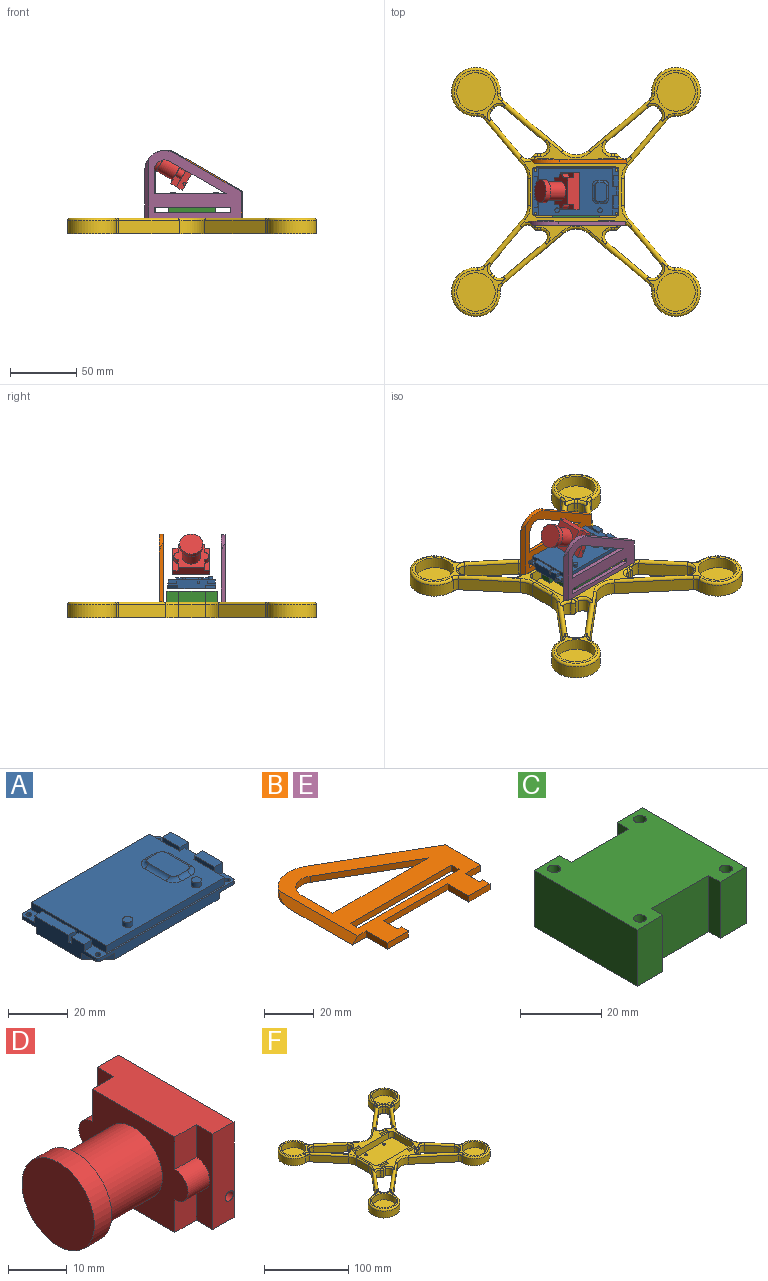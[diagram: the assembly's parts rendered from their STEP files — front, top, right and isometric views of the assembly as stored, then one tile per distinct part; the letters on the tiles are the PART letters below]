
ASSEMBLY  parts=6 mates=2
PART A: 60 faces, bbox 65x36.5x9 mm
  f0: plane 58.7x35.6mm, normal (0,0,1), area 1787.7mm2, adj f1,f24,f25,f26,f27,f29,f31,f48
  f1: plane 15x3mm, normal (1,0,0), area 45mm2, adj f0,f2,f26,f50
  f2: plane 65x36.5mm, normal (0,0,1), area 195mm2, adj f1,f6,f7,f8,f9,f10,f11,f12
  f3: plane 7.67x7.67mm, normal (0,0,-1), area 26mm2, adj f9,f10,f11,f16,f23
  f4: plane 7.67x7.67mm, normal (0,0,-1), area 26mm2, adj f11,f12,f15,f17,f22
  f5: plane 7.67x7.67mm, normal (0,0,-1), area 26mm2, adj f7,f8,f9,f13,f20
  f6: cylinder r=1mm len=1.4mm, axis (0,0,-1), area 2.2mm2, adj f2,f7,f17,f18
  f7: plane 63x4mm, normal (0,1,0), area 217.3mm2, adj f2,f5,f6,f8,f18,f19,f20,f21
  f8: cylinder r=1mm len=1.4mm, axis (0,0,-1), area 2.2mm2, adj f2,f5,f7,f9
  f9: plane 34.5x6.8mm, normal (-1,0,0), area 164.9mm2, adj f2,f3,f5,f8,f10,f19,f20,f23
  f10: cylinder r=1mm len=1.4mm, axis (0,0,-1), area 2.2mm2, adj f2,f3,f9,f11
  f11: plane 63x4mm, normal (0,-1,0), area 217.3mm2, adj f2,f3,f4,f10,f12,f19,f22,f23
  f12: cylinder r=1mm len=1.4mm, axis (0,0,-1), area 2.2mm2, adj f2,f4,f11,f17
  f13: cylinder r=1mm len=2mm, axis (0,0,-1), area 8.8mm2, adj f2,f5
  f14: cylinder r=1mm len=2mm, axis (0,0,-1), area 8.8mm2, adj f2,f18
  f15: cylinder r=1mm len=2mm, axis (0,0,-1), area 8.8mm2, adj f2,f4
  f16: cylinder r=1mm len=2mm, axis (0,0,-1), area 8.8mm2, adj f2,f3
  f17: plane 34.5x8.3mm, normal (1,0,0), area 179.9mm2, adj f2,f4,f6,f12,f18,f19,f21,f22
  f18: plane 7.67x7.67mm, normal (0,0,-1), area 26mm2, adj f6,f7,f14,f17,f21
  f19: plane 65x36.5mm, normal (0,0,-1), area 2254.9mm2, adj f7,f9,f11,f17,f20,f21,f22,f23
  f20: plane 7.67x7.67mm, normal (-0.71,0.71,0), area 28.2mm2, adj f5,f7,f9,f19
  f21: plane 7.67x7.67mm, normal (0.71,0.71,0), area 28.2mm2, adj f7,f17,f18,f19
  f22: plane 7.67x7.67mm, normal (0.71,-0.71,0), area 28.2mm2, adj f4,f11,f17,f19
  f23: plane 7.67x7.67mm, normal (-0.71,-0.71,0), area 28.2mm2, adj f3,f9,f11,f19
  f24: plane 14x3mm, normal (1,0,0), area 42mm2, adj f0,f2,f25,f49
  f25: plane 56x3mm, normal (0,1,0), area 168mm2, adj f0,f2,f24,f27
  f26: plane 56x3mm, normal (0,-1,0), area 168mm2, adj f0,f1,f2,f27
  f27: plane 35.6x3mm, normal (-1,0,0), area 106.8mm2, adj f0,f2,f25,f26
  f28: plane 3.5x3.5mm, normal (0,0,1), area 9.6mm2, adj f29
  f29: cylinder r=1.75mm len=3.5mm, axis (0,0,-1), area 22mm2, adj f0,f28
  f30: plane 3.5x3.5mm, normal (0,0,1), area 9.6mm2, adj f31
  f31: cylinder r=1.75mm len=3.5mm, axis (0,0,-1), area 22mm2, adj f0,f30
  f32: plane 16x3.7mm, normal (0,0,1), area 59.2mm2, adj f9,f33,f34,f35
  f33: plane 3.7x2.8mm, normal (0,1,0), area 10.4mm2, adj f2,f9,f32,f34
  f34: plane 16x2.8mm, normal (1,0,0), area 44.8mm2, adj f2,f32,f33,f35
  f35: plane 3.7x2.8mm, normal (0,-1,0), area 10.4mm2, adj f2,f9,f32,f34
  f36: plane 6x3.7mm, normal (0,0,1), area 22.2mm2, adj f9,f37,f38,f39
  f37: plane 3.7x2.8mm, normal (0,1,0), area 10.4mm2, adj f2,f9,f36,f38
  f38: plane 6x2.8mm, normal (1,0,0), area 16.8mm2, adj f2,f36,f37,f39
  f39: plane 3.7x2.8mm, normal (0,-1,0), area 10.4mm2, adj f2,f9,f36,f38
  f40: plane 9.5x4mm, normal (0,0,1), area 38mm2, adj f17,f41,f42,f43
  f41: plane 4.3x4mm, normal (0,-1,0), area 17.2mm2, adj f2,f17,f40,f42
  f42: plane 9.5x4.3mm, normal (-1,0,0), area 40.9mm2, adj f2,f40,f41,f43
  f43: plane 4.3x4mm, normal (0,1,0), area 17.2mm2, adj f2,f17,f40,f42
  f44: plane 8.3x4mm, normal (0,0,1), area 33.2mm2, adj f17,f45,f46,f47
  f45: plane 4.3x4mm, normal (0,1,0), area 17.2mm2, adj f2,f17,f44,f47
  f46: plane 4.3x4mm, normal (0,-1,0), area 17.2mm2, adj f2,f17,f44,f47
  f47: plane 8.3x4.3mm, normal (-1,0,0), area 35.7mm2, adj f2,f44,f45,f46
  f48: plane 6.6x3mm, normal (1,0,0), area 19.8mm2, adj f0,f2,f49,f50
  f49: plane 3x2.7mm, normal (0,1,0), area 8.1mm2, adj f0,f2,f24,f48
  f50: plane 3x2.7mm, normal (0,-1,0), area 8.1mm2, adj f0,f1,f2,f48
  f51: plane 14x8.5mm, normal (0,0,1), area 115.6mm2, adj f52,f53,f54,f55,f56,f57,f58,f59
  f52: cylinder r=2mm len=4.5mm, axis (1,0,0), area 10.9mm2, adj f0,f51,f53,f54
  f53: torus R=3.87mm, axis (0,0,1), area 10.7mm2, adj f0,f51,f52,f55
  f54: torus R=3.87mm, axis (0,0,1), area 10.7mm2, adj f0,f51,f52,f56
  f55: cylinder r=2mm len=10mm, axis (0,1,0), area 24.3mm2, adj f0,f51,f53,f57
  f56: cylinder r=2mm len=10mm, axis (0,-1,0), area 24.3mm2, adj f0,f51,f54,f58
  f57: torus R=3.87mm, axis (0,0,1), area 10.7mm2, adj f0,f51,f55,f59
  f58: torus R=3.87mm, axis (0,0,1), area 10.7mm2, adj f0,f51,f56,f59
  f59: cylinder r=2mm len=4.5mm, axis (1,0,0), area 10.9mm2, adj f0,f51,f57,f58
PART B: 28 faces, bbox 73x63.1x3 mm
  f0: plane 8x3mm, normal (1,0,0), area 24mm2, adj f1,f24,f25,f26
  f1: plane 36.5x3mm, normal (0,-1,0), area 109.5mm2, adj f0,f2,f25,f26
  f2: plane 12x3mm, normal (-1,0,0), area 36mm2, adj f1,f3,f25,f26
  f3: plane 12x3mm, normal (0,-1,0), area 36mm2, adj f2,f4,f25,f26
  f4: plane 4x3mm, normal (1,0,0), area 12mm2, adj f3,f5,f25,f26
  f5: plane 3x2mm, normal (0,1,0), area 6mm2, adj f4,f6,f25,f26
  f6: plane 8x3mm, normal (1,0,0), area 24mm2, adj f5,f7,f25,f26
  f7: plane 8.5x3mm, normal (0,-1,0), area 25.5mm2, adj f6,f8,f25,f26
  f8: plane 20x3mm, normal (1,0,0), area 60mm2, adj f7,f9,f25,f26
  f9: plane 50.41x29.1mm, normal (0.5,0.87,0), area 174.6mm2, adj f8,f10,f25,f26
  f10: cylinder r=15mm len=22.43mm, axis (0,0,-1), area 75.8mm2, adj f9,f11,f25,f26,f27
  f11: cylinder r=33.51mm len=3.32mm, axis (0,0,-1), area 0.2mm2, adj f10,f26,f27
  f12: plane 8x3mm, normal (0,-1,0), area 19.5mm2, adj f13,f25,f26,f27
  f13: plane 12x3mm, normal (-1,0,0), area 36mm2, adj f12,f14,f25,f26
  f14: plane 12x3mm, normal (0,-1,0), area 36mm2, adj f13,f15,f25,f26
  f15: plane 4x3mm, normal (1,0,0), area 12mm2, adj f14,f24,f25,f26
  f16: plane 4.38x3mm, normal (-1,0,0), area 13.1mm2, adj f17,f22,f25,f26
  f17: plane 57.57x3mm, normal (0,1,0), area 172.7mm2, adj f16,f18,f25,f26
  f18: plane 4.38x3mm, normal (1,0,0), area 13.1mm2, adj f17,f22,f25,f26
  f19: plane 54.56x3mm, normal (0,1,0), area 163.7mm2, adj f20,f23,f25,f26
  f20: plane 17.86x3mm, normal (1,0,0), area 53.6mm2, adj f19,f21,f25,f26
  f21: cylinder r=7.88mm len=11.82mm, axis (0,0,-1), area 49.5mm2, adj f20,f23,f25,f26
  f22: plane 57.57x3mm, normal (0,-1,0), area 172.7mm2, adj f16,f18,f25,f26
  f23: plane 42.74x24.68mm, normal (-0.5,-0.87,0), area 148.1mm2, adj f19,f21,f25,f26
  f24: plane 3x2mm, normal (0,1,0), area 6mm2, adj f0,f15,f25,f26
  f25: plane 70x63.11mm, normal (0,0,1), area 1903.1mm2, adj f0,f1,f2,f3,f4,f5,f6,f7
  f26: plane 73x63.11mm, normal (0,0,-1), area 2029mm2, adj f0,f1,f2,f3,f4,f5,f6,f7
  f27: plane 44.99x3mm, normal (-0.71,0,0.71), area 178.1mm2, adj f10,f11,f12,f25,f26
PART C: 18 faces, bbox 38x36x17 mm
  f0: plane 36x17.02mm, normal (1,0,0), area 612.6mm2, adj f1,f15,f16,f17
  f1: plane 17.02x9mm, normal (0,1,0), area 153.2mm2, adj f0,f2,f16,f17
  f2: plane 17.02x4mm, normal (-1,0,0), area 68.1mm2, adj f1,f3,f16,f17
  f3: plane 20x17.02mm, normal (0,1,0), area 340.4mm2, adj f2,f4,f16,f17
  f4: plane 17.02x4mm, normal (1,0,0), area 68.1mm2, adj f3,f5,f16,f17
  f5: plane 17.02x9mm, normal (0,1,0), area 153.2mm2, adj f4,f6,f16,f17
  f6: plane 36x17.02mm, normal (-1,0,0), area 612.6mm2, adj f5,f7,f16,f17
  f7: plane 17.02x9mm, normal (0,-1,0), area 153.2mm2, adj f6,f8,f16,f17
  f8: plane 17.02x4mm, normal (1,0,0), area 68.1mm2, adj f7,f9,f16,f17
  f9: plane 20x17.02mm, normal (0,-1,0), area 340.4mm2, adj f8,f10,f16,f17
  f10: plane 17.02x4mm, normal (-1,0,0), area 68.1mm2, adj f9,f15,f16,f17
  f11: cylinder r=1.6mm len=17.02mm, axis (0,0,-1), area 171.1mm2, adj f16,f17
  f12: cylinder r=1.6mm len=17.02mm, axis (0,0,-1), area 171.1mm2, adj f16,f17
  f13: cylinder r=1.6mm len=17.02mm, axis (0,0,-1), area 171.1mm2, adj f16,f17
  f14: cylinder r=1.6mm len=17.02mm, axis (0,0,-1), area 171.1mm2, adj f16,f17
  f15: plane 17.02x9mm, normal (0,-1,0), area 153.2mm2, adj f0,f10,f16,f17
  f16: plane 38x36mm, normal (0,0,1), area 1175.8mm2, adj f0,f1,f2,f3,f4,f5,f6,f7
  f17: plane 38x36mm, normal (0,0,-1), area 1175.8mm2, adj f0,f1,f2,f3,f4,f5,f6,f7
PART D: 22 faces, bbox 28.5x28.2x20 mm
  f0: plane 20x4.16mm, normal (-1,0,0), area 63.9mm2, adj f2,f4,f6,f12,f16,f17
  f1: plane 20x4mm, normal (-1,0,0), area 63.9mm2, adj f2,f5,f6,f13,f14,f15
  f2: plane 28x10.3mm, normal (0,0,1), area 246.8mm2, adj f0,f1,f3,f4,f5,f11,f15,f16
  f3: plane 28x20mm, normal (1,0,0), area 560mm2, adj f2,f4,f5,f6
  f4: plane 20x5.1mm, normal (0,1,0), area 98.9mm2, adj f0,f2,f3,f6,f10
  f5: plane 20x5.1mm, normal (0,-1,0), area 98.9mm2, adj f1,f2,f3,f6,f8
  f6: plane 28x10.3mm, normal (0,0,-1), area 246.8mm2, adj f0,f1,f3,f4,f5,f11,f12,f13
  f7: plane 2x2mm, normal (0,-1,0), area 3.1mm2, adj f8
  f8: cylinder r=1mm len=3mm, axis (0,-1,0), area 18.8mm2, adj f5,f7
  f9: plane 2x2mm, normal (0,1,0), area 3.1mm2, adj f10
  f10: cylinder r=1mm len=3mm, axis (0,1,0), area 18.8mm2, adj f4,f9
  f11: plane 27.36x20mm, normal (-1,0,0), area 278.2mm2, adj f2,f6,f12,f13,f14,f15,f16,f17
  f12: plane 6.8x5.2mm, normal (0,1,0), area 35.4mm2, adj f0,f6,f11,f17
  f13: plane 6.8x5.2mm, normal (0,-1,0), area 35.4mm2, adj f1,f6,f11,f14
  f14: cylinder r=3.2mm len=6.4mm, axis (1,0,0), area 52.3mm2, adj f1,f11,f13,f15
  f15: plane 6.8x5.2mm, normal (0,-1,0), area 35.4mm2, adj f1,f2,f11,f14
  f16: plane 6.8x5.2mm, normal (0,1,0), area 35.4mm2, adj f0,f2,f11,f17
  f17: extruded ~6.4x5.2mm, area 52.3mm2, adj f0,f11,f12,f16
  f18: cylinder r=7mm len=14mm, axis (1,0,0), area 615.8mm2, adj f11,f21
  f19: plane 17.5x17.5mm, normal (-1,0,0), area 240.5mm2, adj f20
  f20: cylinder r=8.75mm len=17.5mm, axis (1,0,0), area 230.9mm2, adj f19,f21
  f21: plane 17.5x17.5mm, normal (1,0,0), area 86.6mm2, adj f18,f20
PART E: same geometry as B
PART F: 171 faces, bbox 191.4x191.4x12 mm
  f0: plane 8x3.5mm, normal (-1,0,0), area 28mm2, adj f7,f55,f57,f170
  f1: plane 8x3.5mm, normal (-1,0,0), area 28mm2, adj f7,f59,f60,f168
  f2: plane 8x3.5mm, normal (-1,0,0), area 28mm2, adj f7,f62,f63,f164
  f3: plane 8x3.5mm, normal (-1,0,0), area 28mm2, adj f7,f64,f66,f166
  f4: plane 38.79x38.79mm, normal (0,0,1), area 226.8mm2, adj f46,f122,f126,f129,f133,f137,f157,f159
  f5: plane 38.79x38.79mm, normal (0,0,1), area 226.8mm2, adj f48,f141,f144,f147,f148,f151,f152,f154
  f6: plane 38.79x38.79mm, normal (0,0,1), area 226.8mm2, adj f44,f124,f127,f130,f131,f134,f135,f138
  f7: plane 84.28x78.72mm, normal (0,0,1), area 1391.4mm2, adj f0,f1,f2,f3,f25,f26,f27,f28
  f8: plane 38.79x38.79mm, normal (0,0,1), area 226.8mm2, adj f50,f108,f109,f111,f112,f115,f116,f119
  f9: plane 188.37x188.37mm, normal (0,0,-1), area 10299.6mm2, adj f10,f11,f12,f13,f14,f15,f16,f17
  f10: plane 35.64x29.9mm, normal (0.77,0.64,0), area 465.2mm2, adj f9,f34,f39,f139
  f11: plane 35.64x29.9mm, normal (0.77,-0.64,0), area 465.2mm2, adj f9,f35,f40,f154
  f12: plane 45.79x38.42mm, normal (-0.64,0.77,0), area 597.7mm2, adj f9,f36,f41,f141
  f13: plane 45.79x38.42mm, normal (0.64,0.77,0), area 597.7mm2, adj f9,f29,f41,f137
  f14: cylinder r=18.53mm len=37.05mm, axis (0,0,-1), area 903.2mm2, adj f9,f29,f30,f129
  f15: plane 35.64x29.9mm, normal (-0.77,-0.64,0), area 465.2mm2, adj f9,f30,f37,f122
  f16: plane 35.64x29.9mm, normal (-0.77,0.64,0), area 465.2mm2, adj f9,f31,f38,f108
  f17: cylinder r=18.53mm len=37.05mm, axis (0,0,-1), area 903.2mm2, adj f9,f31,f32,f115
  f18: plane 45.79x38.42mm, normal (0.64,-0.77,0), area 597.7mm2, adj f9,f32,f42,f120
  f19: plane 45.79x38.42mm, normal (-0.64,-0.77,0), area 597.7mm2, adj f9,f33,f42,f124
  f20: cylinder r=18.53mm len=37.05mm, axis (0,0,-1), area 903.2mm2, adj f9,f33,f34,f134
  f21: cylinder r=18.53mm len=37.05mm, axis (0,0,-1), area 903.2mm2, adj f9,f35,f36,f152
  f22: plane 20.3x10mm, normal (1,0,0), area 203mm2, adj f9,f39,f40,f149
  f23: plane 20.3x10mm, normal (-1,0,0), area 203mm2, adj f9,f37,f38,f118
  f24: plane 65x39mm, normal (0,0,1), area 2481.4mm2, adj f25,f26,f27,f28,f51,f52,f53,f54
  f25: plane 29x9mm, normal (1,0,0), area 261mm2, adj f7,f24,f51,f53
  f26: plane 55x9mm, normal (0,1,0), area 495mm2, adj f7,f24,f51,f52
  f27: plane 29x9mm, normal (-1,0,0), area 261mm2, adj f7,f24,f52,f54
  f28: plane 55x9mm, normal (0,-1,0), area 495mm2, adj f7,f24,f53,f54
  f29: cylinder r=5mm len=10mm, axis (0,0,-1), area 47.7mm2, adj f9,f13,f14,f133
  f30: cylinder r=5mm len=10mm, axis (0,0,-1), area 47.7mm2, adj f9,f14,f15,f126
  f31: cylinder r=5mm len=10mm, axis (0,0,-1), area 47.7mm2, adj f9,f16,f17,f111
  f32: cylinder r=5mm len=10mm, axis (0,0,-1), area 47.7mm2, adj f9,f17,f18,f119
  f33: cylinder r=5mm len=10mm, axis (0,0,-1), area 47.7mm2, adj f9,f19,f20,f130
  f34: cylinder r=5mm len=10mm, axis (0,0,-1), area 47.7mm2, adj f9,f10,f20,f138
  f35: cylinder r=5mm len=10mm, axis (0,0,-1), area 47.7mm2, adj f9,f11,f21,f155
  f36: cylinder r=5mm len=10mm, axis (0,0,-1), area 47.7mm2, adj f9,f12,f21,f148
  f37: cylinder r=15mm len=10mm, axis (0,0,1), area 104.7mm2, adj f9,f15,f23,f121
  f38: cylinder r=15mm len=10mm, axis (0,0,-1), area 104.7mm2, adj f9,f16,f23,f114
  f39: cylinder r=15mm len=10mm, axis (0,0,1), area 104.7mm2, adj f9,f10,f22,f145
  f40: cylinder r=15mm len=10mm, axis (0,0,-1), area 104.7mm2, adj f9,f11,f22,f153
  f41: cylinder r=15mm len=19.28mm, axis (0,0,-1), area 209.4mm2, adj f9,f12,f13,f142
  f42: cylinder r=15mm len=19.28mm, axis (0,0,-1), area 209.4mm2, adj f9,f18,f19,f123
  f43: plane 29.05x29.05mm, normal (0,0,1), area 662.8mm2, adj f44
  f44: cylinder r=14.53mm len=29.05mm, axis (0,0,1), area 821.4mm2, adj f6,f43
  f45: plane 29.05x29.05mm, normal (0,0,1), area 662.8mm2, adj f46
  f46: cylinder r=14.53mm len=29.05mm, axis (0,0,1), area 821.4mm2, adj f4,f45
  f47: plane 29.05x29.05mm, normal (0,0,1), area 662.8mm2, adj f48
  f48: cylinder r=14.53mm len=29.05mm, axis (0,0,1), area 821.4mm2, adj f5,f47
  f49: plane 29.05x29.05mm, normal (0,0,1), area 662.8mm2, adj f50
  f50: cylinder r=14.53mm len=29.05mm, axis (0,0,1), area 821.4mm2, adj f8,f49
  f51: cylinder r=5mm len=9mm, axis (0,0,-1), area 70.7mm2, adj f7,f24,f25,f26
  f52: cylinder r=5mm len=9mm, axis (0,0,1), area 70.7mm2, adj f7,f24,f26,f27
  f53: cylinder r=5mm len=9mm, axis (0,0,1), area 70.7mm2, adj f7,f24,f25,f28
  f54: cylinder r=5mm len=9mm, axis (0,0,-1), area 70.7mm2, adj f7,f24,f27,f28
  f55: plane 16x12mm, normal (0,-1,0), area 160mm2, adj f0,f7,f9,f56,f169,f170
  f56: plane 12x3.5mm, normal (1,0,0), area 42mm2, adj f7,f9,f55,f57
  f57: plane 16x12mm, normal (0,1,0), area 160mm2, adj f0,f7,f9,f56,f169,f170
  f58: plane 12x3.5mm, normal (1,0,0), area 42mm2, adj f7,f9,f59,f60
  f59: plane 16x12mm, normal (0,1,0), area 160mm2, adj f1,f7,f9,f58,f167,f168
  f60: plane 16x12mm, normal (0,-1,0), area 160mm2, adj f1,f7,f9,f58,f167,f168
  f61: plane 12x3.5mm, normal (1,0,0), area 42mm2, adj f7,f9,f62,f63
  f62: plane 16x12mm, normal (0,1,0), area 160mm2, adj f2,f7,f9,f61,f163,f164
  f63: plane 16x12mm, normal (0,-1,0), area 160mm2, adj f2,f7,f9,f61,f163,f164
  f64: plane 16x12mm, normal (0,-1,0), area 160mm2, adj f3,f7,f9,f65,f165,f166
  f65: plane 12x3.5mm, normal (1,0,0), area 42mm2, adj f7,f9,f64,f66
  f66: plane 16x12mm, normal (0,1,0), area 160mm2, adj f3,f7,f9,f65,f165,f166
  f67: cylinder r=1.6mm len=3.2mm, axis (0,0,-1), area 30.2mm2, adj f9,f24
  f68: cylinder r=1.6mm len=3.2mm, axis (0,0,-1), area 30.2mm2, adj f9,f24
  f69: cylinder r=1.6mm len=3.2mm, axis (0,0,-1), area 30.2mm2, adj f9,f24
  f70: cylinder r=1.6mm len=3.2mm, axis (0,0,-1), area 30.2mm2, adj f9,f24
  f71: cylinder r=18.53mm len=10mm, axis (0,0,1), area 26.1mm2, adj f9,f103,f106,f159
  f72: plane 27.96x23.46mm, normal (0.77,0.64,0), area 365mm2, adj f9,f105,f106,f122
  f73: plane 10x2.62mm, normal (0,1,0), area 26.2mm2, adj f9,f90,f104,f158
  f74: plane 31.27x26.24mm, normal (-0.64,-0.77,0), area 408.2mm2, adj f9,f103,f104,f137
  f75: cylinder r=18.53mm len=10mm, axis (0,0,1), area 26.1mm2, adj f9,f91,f94,f131
  f76: plane 27.96x23.46mm, normal (-0.77,-0.64,0), area 365mm2, adj f9,f93,f94,f139
  f77: plane 10x2.62mm, normal (0,-1,0), area 26.2mm2, adj f9,f87,f92,f128
  f78: plane 31.27x26.24mm, normal (0.64,0.77,0), area 408.2mm2, adj f9,f91,f92,f124
  f79: plane 27.96x23.46mm, normal (-0.77,0.64,0), area 365mm2, adj f9,f95,f98,f154
  f80: cylinder r=18.53mm len=10mm, axis (0,0,1), area 26.1mm2, adj f9,f97,f98,f147
  f81: plane 31.27x26.24mm, normal (0.64,-0.77,0), area 408.2mm2, adj f9,f96,f97,f141
  f82: plane 10x2.62mm, normal (0,1,0), area 26.2mm2, adj f9,f88,f96,f143
  f83: plane 27.96x23.46mm, normal (0.77,-0.64,0), area 365mm2, adj f9,f99,f102,f108
  f84: cylinder r=18.53mm len=10mm, axis (0,0,1), area 26.1mm2, adj f9,f99,f100,f112
  f85: plane 31.27x26.24mm, normal (-0.64,0.77,0), area 408.2mm2, adj f9,f100,f101,f120
  f86: plane 10x2.62mm, normal (0,-1,0), area 26.2mm2, adj f9,f89,f101,f113
  f87: cylinder r=4mm len=10mm, axis (0,0,1), area 39.6mm2, adj f9,f77,f93,f132
  f88: cylinder r=4mm len=10mm, axis (0,0,1), area 39.6mm2, adj f9,f82,f95,f146
  f89: cylinder r=4mm len=10mm, axis (0,0,1), area 39.6mm2, adj f9,f86,f102,f110
  f90: cylinder r=4mm len=10mm, axis (0,0,1), area 39.6mm2, adj f9,f73,f105,f160
  f91: cylinder r=5mm len=10mm, axis (0,0,1), area 77.7mm2, adj f9,f75,f78,f127
  f92: cylinder r=5mm len=10mm, axis (0,0,-1), area 122.2mm2, adj f9,f77,f78,f125
  f93: cylinder r=5mm len=10mm, axis (0,0,1), area 93.1mm2, adj f9,f76,f87,f136
  f94: cylinder r=5mm len=10mm, axis (0,0,1), area 77.7mm2, adj f9,f75,f76,f135
  f95: cylinder r=5mm len=10mm, axis (0,0,1), area 93.1mm2, adj f9,f79,f88,f150
  f96: cylinder r=5mm len=10mm, axis (0,0,-1), area 122.2mm2, adj f9,f81,f82,f140
  f97: cylinder r=5mm len=10mm, axis (0,0,1), area 77.7mm2, adj f9,f80,f81,f144
  f98: cylinder r=5mm len=10mm, axis (0,0,1), area 77.7mm2, adj f9,f79,f80,f151
  f99: cylinder r=5mm len=10mm, axis (0,0,1), area 77.7mm2, adj f9,f83,f84,f109
  f100: cylinder r=5mm len=10mm, axis (0,0,1), area 77.7mm2, adj f9,f84,f85,f116
  f101: cylinder r=5mm len=10mm, axis (0,0,-1), area 122.2mm2, adj f9,f85,f86,f117
  f102: cylinder r=5mm len=10mm, axis (0,0,1), area 93.1mm2, adj f9,f83,f89,f107
  f103: cylinder r=5mm len=10mm, axis (0,0,1), area 77.7mm2, adj f9,f71,f74,f157
  f104: cylinder r=5mm len=10mm, axis (0,0,-1), area 122.2mm2, adj f9,f73,f74,f156
  f105: cylinder r=5mm len=10mm, axis (0,0,1), area 93.1mm2, adj f9,f72,f90,f162
  f106: cylinder r=5mm len=10mm, axis (0,0,1), area 77.7mm2, adj f9,f71,f72,f161
  f107: torus R=7mm, axis (0,0,1), area 33.5mm2, adj f7,f102,f108,f110
  f108: cylinder r=2mm len=38.21mm, axis (0.64,0.77,0), area 260.8mm2, adj f7,f8,f16,f83,f107,f109,f111,f114
  f109: torus R=7mm, axis (0,0,1), area 28mm2, adj f8,f99,f108,f112
  f110: torus R=2mm, axis (0,0,1), area 10.2mm2, adj f7,f89,f107,f113
  f111: torus R=7mm, axis (0,0,1), area 17.2mm2, adj f8,f31,f108,f115
  f112: torus R=16.53mm, axis (0,0,1), area 7.9mm2, adj f8,f84,f109,f116
  f113: cylinder r=2mm len=2.62mm, axis (1,0,0), area 8.2mm2, adj f7,f86,f110,f117
  f114: torus R=17mm, axis (0,0,1), area 34.5mm2, adj f7,f38,f108,f118
  f115: torus R=16.53mm, axis (0,0,1), area 272.6mm2, adj f8,f17,f111,f119
  f116: torus R=7mm, axis (0,0,1), area 28mm2, adj f8,f100,f112,f120
  f117: torus R=7mm, axis (0,0,1), area 44mm2, adj f7,f101,f113,f120
  f118: cylinder r=2mm len=20.3mm, axis (0,1,0), area 63.8mm2, adj f7,f23,f114,f121
  f119: torus R=7mm, axis (0,0,1), area 17.2mm2, adj f8,f32,f115,f120
  f120: cylinder r=2mm len=48.36mm, axis (-0.77,-0.64,0), area 316mm2, adj f7,f8,f18,f85,f116,f117,f119,f123
  f121: torus R=17mm, axis (0,0,1), area 34.5mm2, adj f7,f37,f118,f122
  f122: cylinder r=2mm len=38.21mm, axis (-0.64,0.77,0), area 260.8mm2, adj f4,f7,f15,f72,f121,f126,f161,f162
  f123: torus R=17mm, axis (0,0,1), area 69mm2, adj f7,f42,f120,f124
  f124: cylinder r=2mm len=48.36mm, axis (-0.77,0.64,0), area 316mm2, adj f6,f7,f19,f78,f123,f125,f127,f130
  f125: torus R=7mm, axis (0,0,1), area 44mm2, adj f7,f92,f124,f128
  f126: torus R=7mm, axis (0,0,1), area 17.2mm2, adj f4,f30,f122,f129
  f127: torus R=7mm, axis (0,0,1), area 28mm2, adj f6,f91,f124,f131
  f128: cylinder r=2mm len=2.62mm, axis (1,0,0), area 8.2mm2, adj f7,f77,f125,f132
  f129: torus R=16.53mm, axis (0,0,1), area 272.6mm2, adj f4,f14,f126,f133
  f130: torus R=7mm, axis (0,0,1), area 17.2mm2, adj f6,f33,f124,f134
  f131: torus R=16.53mm, axis (0,0,1), area 7.9mm2, adj f6,f75,f127,f135
  f132: torus R=2mm, axis (0,0,1), area 10.2mm2, adj f7,f87,f128,f136
  f133: torus R=7mm, axis (0,0,1), area 17.2mm2, adj f4,f29,f129,f137
  f134: torus R=16.53mm, axis (0,0,1), area 272.6mm2, adj f6,f20,f130,f138
  f135: torus R=7mm, axis (0,0,1), area 28mm2, adj f6,f94,f131,f139
  f136: torus R=7mm, axis (0,0,1), area 33.5mm2, adj f7,f93,f132,f139
  f137: cylinder r=2mm len=48.36mm, axis (0.77,-0.64,0), area 316mm2, adj f4,f7,f13,f74,f133,f142,f156,f157
  f138: torus R=7mm, axis (0,0,1), area 17.2mm2, adj f6,f34,f134,f139
  f139: cylinder r=2mm len=38.21mm, axis (0.64,-0.77,0), area 260.8mm2, adj f6,f7,f10,f76,f135,f136,f138,f145
  f140: torus R=7mm, axis (0,0,1), area 44mm2, adj f7,f96,f141,f143
  f141: cylinder r=2mm len=48.36mm, axis (0.77,0.64,0), area 316mm2, adj f5,f7,f12,f81,f140,f142,f144,f148
  f142: torus R=17mm, axis (0,0,1), area 69mm2, adj f7,f41,f137,f141
  f143: cylinder r=2mm len=2.62mm, axis (-1,0,0), area 8.2mm2, adj f7,f82,f140,f146
  f144: torus R=7mm, axis (0,0,1), area 28mm2, adj f5,f97,f141,f147
  f145: torus R=17mm, axis (0,0,1), area 34.5mm2, adj f7,f39,f139,f149
  f146: torus R=2mm, axis (0,0,1), area 10.2mm2, adj f7,f88,f143,f150
  f147: torus R=16.53mm, axis (0,0,1), area 7.9mm2, adj f5,f80,f144,f151
  f148: torus R=7mm, axis (0,0,1), area 17.2mm2, adj f5,f36,f141,f152
  f149: cylinder r=2mm len=20.3mm, axis (0,-1,0), area 63.8mm2, adj f7,f22,f145,f153
  f150: torus R=7mm, axis (0,0,1), area 33.5mm2, adj f7,f95,f146,f154
  f151: torus R=7mm, axis (0,0,1), area 28mm2, adj f5,f98,f147,f154
  f152: torus R=16.53mm, axis (0,0,1), area 272.6mm2, adj f5,f21,f148,f155
  f153: torus R=17mm, axis (0,0,1), area 34.5mm2, adj f7,f40,f149,f154
  f154: cylinder r=2mm len=38.21mm, axis (-0.64,-0.77,0), area 260.8mm2, adj f5,f7,f11,f79,f150,f151,f153,f155
  f155: torus R=7mm, axis (0,0,1), area 17.2mm2, adj f5,f35,f152,f154
  f156: torus R=7mm, axis (0,0,1), area 44mm2, adj f7,f104,f137,f158
  f157: torus R=7mm, axis (0,0,1), area 28mm2, adj f4,f103,f137,f159
  f158: cylinder r=2mm len=2.62mm, axis (-1,0,0), area 8.2mm2, adj f7,f73,f156,f160
  f159: torus R=16.53mm, axis (0,0,1), area 7.9mm2, adj f4,f71,f157,f161
  f160: torus R=2mm, axis (0,0,1), area 10.2mm2, adj f7,f90,f158,f162
  f161: torus R=7mm, axis (0,0,1), area 28mm2, adj f4,f106,f122,f159
  f162: torus R=7mm, axis (0,0,1), area 33.5mm2, adj f7,f105,f122,f160
  f163: plane 4x3.5mm, normal (-1,0,0), area 14mm2, adj f9,f62,f63,f164
  f164: plane 4x3.5mm, normal (0,0,-1), area 14mm2, adj f2,f62,f63,f163
  f165: plane 4x3.5mm, normal (-1,0,0), area 14mm2, adj f9,f64,f66,f166
  f166: plane 4x3.5mm, normal (0,0,-1), area 14mm2, adj f3,f64,f66,f165
  f167: plane 4x3.5mm, normal (-1,0,0), area 14mm2, adj f9,f59,f60,f168
  f168: plane 4x3.5mm, normal (0,0,-1), area 14mm2, adj f1,f59,f60,f167
  f169: plane 4x3.5mm, normal (-1,0,0), area 14mm2, adj f9,f55,f57,f170
  f170: plane 4x3.5mm, normal (0,0,-1), area 14mm2, adj f0,f55,f57,f169
PLACE A t=(-0.03,0.18,62.55)mm
PLACE B rot(axis=(1,0,0),90deg) t=(19.74,24.79,36.29)mm
PLACE C rot(axis=(0,0,1),90deg) t=(0,0,39.04)mm
PLACE D rot(axis=(0,1,0),30deg) t=(-14.32,0.53,84.58)mm
PLACE E rot(axis=(1,0,0),90deg) t=(18.67,-22.13,36.04)mm
PLACE F t=(0,0,36.04)mm
MATE planar E.f24 <-> F.f164  axis (0,0,1) through (-16.83,-23.63,40.04)mm
MATE revolute C.f11 <-> F.f67  axis (0,0,-1) through (-15,-15,39.04)mm
